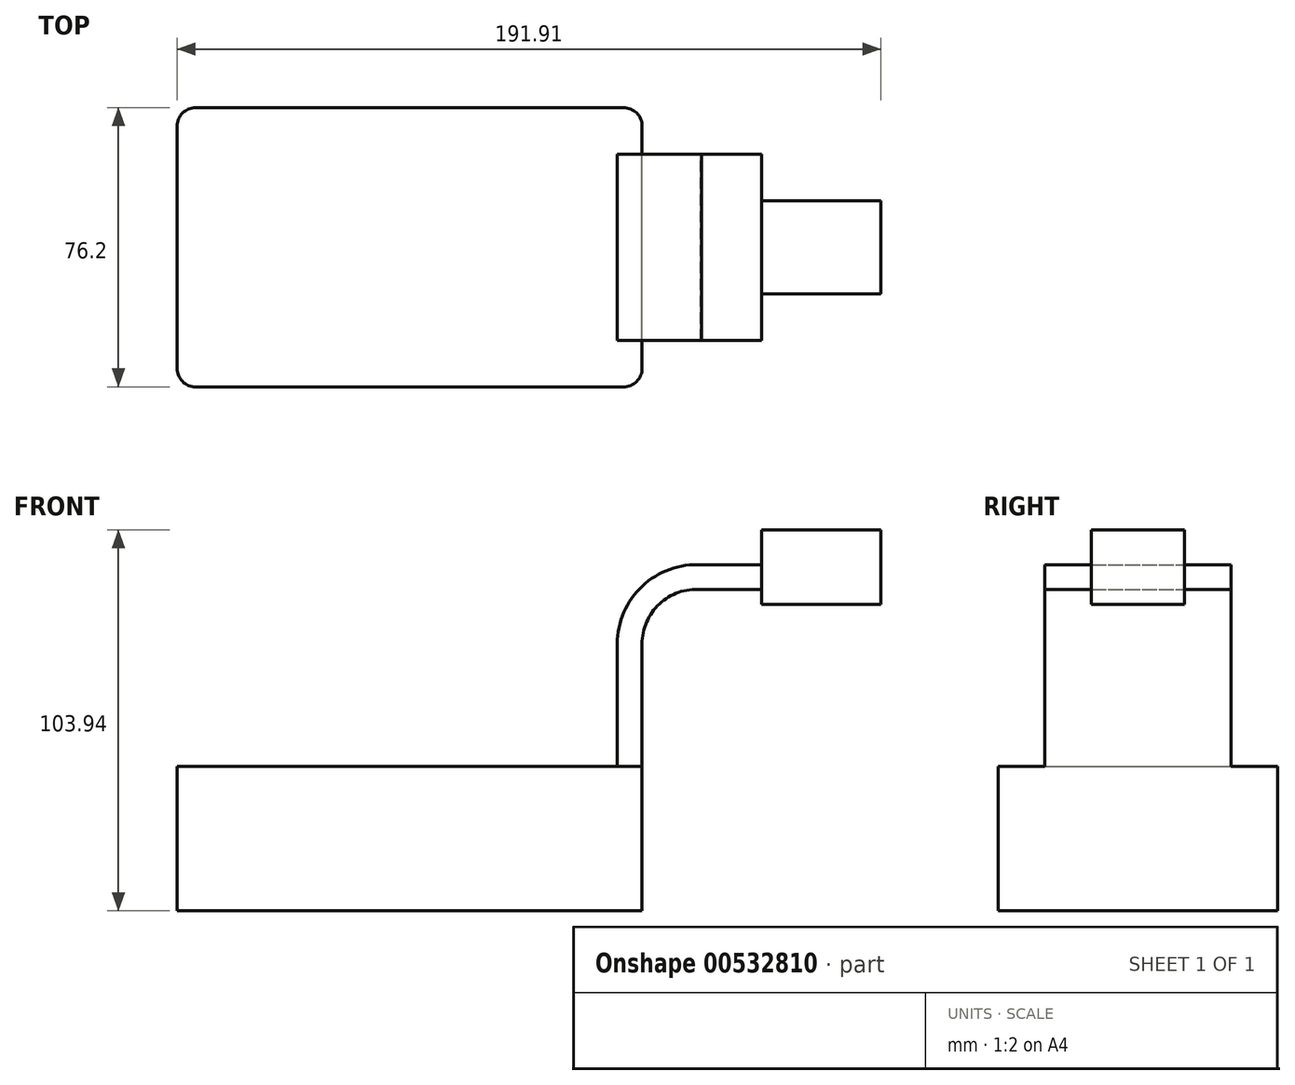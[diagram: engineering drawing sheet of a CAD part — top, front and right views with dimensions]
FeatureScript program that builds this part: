
annotation { "Feature Type Name" : "Feature", "Feature Type Description" : "" }
export const myFeature = defineFeature(function(context is Context, id is Id, definition is map)
    precondition{}
    {
        {
            var Q0;
            Q0=qCreatedBy(makeId("Front.planeOp"),FACE);
            var sketch = newSketch(context, id + "F0", { "sketchPlane" : qUnion([Q0])});
            skLineSegment(sketch, "E0.bottom", {"start": v(-63.4, -19.7) * mm, "end": v(63.4, -19.7) * mm});
            skLineSegment(sketch, "E0.top", {"start": v(-63.4, 19.7) * mm, "end": v(63.4, 19.7) * mm});
            skLineSegment(sketch, "E0.left", {"start": v(-63.4, -19.7) * mm, "end": v(-63.4, 19.7) * mm});
            skLineSegment(sketch, "E0.right", {"start": v(63.4, -19.7) * mm, "end": v(63.4, 19.7) * mm});
            skPoint(sketch, "E0.middle", {"position": v(0, 0) * mm});
            skLineSegment(sketch, "E1.bottom", {"start": v(95.95, 63.92) * mm, "end": v(128.5, 63.92) * mm});
            skLineSegment(sketch, "E1.top", {"start": v(95.95, 84.24) * mm, "end": v(128.5, 84.24) * mm});
            skLineSegment(sketch, "E1.left", {"start": v(95.95, 63.92) * mm, "end": v(95.95, 84.24) * mm});
            skLineSegment(sketch, "E1.right", {"start": v(128.5, 63.92) * mm, "end": v(128.5, 84.24) * mm});
            skPoint(sketch, "E1.middle", {"position": v(112.23, 74.08) * mm});
            skLineSegment(sketch, "E2", {"start": v(63.4, 19.7) * mm, "end": v(63.4, 53.12) * mm});
            skArc(sketch, "E3", {"start": v(63.4, 53.12) * mm, "mid": v(68.16, 64.03) * mm, "end": v(79.39, 67.97) * mm});
            skLineSegment(sketch, "E4", {"start": v(79.39, 67.97) * mm, "end": v(118.23, 67.97) * mm});
            skLineSegment(sketch, "E5.0", {"start": v(79.62, 74.71) * mm, "end": v(118.23, 74.71) * mm});
            skArc(sketch, "E5.1", {"start": v(56.65, 53.12) * mm, "mid": v(63.47, 68.88) * mm, "end": v(79.62, 74.71) * mm});
            skLineSegment(sketch, "E5.2", {"start": v(56.65, 19.7) * mm, "end": v(56.65, 53.12) * mm});
            skFitSpline(sketch, "E6", {"points": [v(-63.4, 19.7) * mm, v(95.95, 84.24) * mm], "startDerivative": vector(174.77, 0) * mm, "endDerivative": vector(220.18, -72.82) * mm});
            skSolve(sketch);
        }
        {
            var Q0;
            Q0=makeQuery(id+"F0.imprint","IMPRINT",FACE,{"disambiguationData":[TD([[makeQuery(id+"F0.imprint","IMPRINT",EDGE,{"derivedFrom":sQuery(id+"F0.wireOp",EDGE,"E0.bottom")}),1.0]])]});
            extrude(context, id + "F1", {"entities" : qUnion([Q0]), "endBound" : BoundingType.SYMMETRIC, "depth" : 76.2 * mm, "offsetDistance" : 25.4 * mm});
        }
        {
            var Q0;
            {var subQ0=sQuery(id+"F0.wireOp",EDGE,"E5.1");Q0=makeQuery(id+"F0.imprint","IMPRINT",FACE,{"disambiguationData":[TD([[makeQuery(id+"F0.imprint","IMPRINT",EDGE,{"derivedFrom":subQ0}),1.0]])]});}
            extrude(context, id + "F2", {"entities" : qUnion([Q0]), "operationType" : NewBodyOperationType.ADD, "endBound" : BoundingType.SYMMETRIC, "depth" : 50.8 * mm, "offsetDistance" : 25.4 * mm});
        }
        {
            var Q0;
            {var subQ0=sQuery(id+"F0.wireOp",EDGE,"E2");Q0=makeQuery(id+"F0.imprint","IMPRINT",FACE,{"disambiguationData":[TD([[makeQuery(id+"F0.imprint","IMPRINT",EDGE,{"derivedFrom":subQ0}),1.0]])]});}
            extrude(context, id + "F3", {"entities" : qUnion([Q0]), "operationType" : NewBodyOperationType.ADD, "endBound" : BoundingType.SYMMETRIC, "depth" : 25.4 * mm, "offsetDistance" : 25.4 * mm});
        }
        {
            var Q0;
            {var subQ3=sQuery(id+"F0.wireOp",EDGE,"E1.bottom");Q0=makeQuery(id+"F0.imprint","IMPRINT",FACE,{"disambiguationData":[TD([[makeQuery(id+"F0.imprint","IMPRINT",EDGE,{"derivedFrom":subQ3}),1.0]])]});}
            extrude(context, id + "F4", {"entities" : qUnion([Q0]), "operationType" : NewBodyOperationType.ADD, "endBound" : BoundingType.SYMMETRIC, "depth" : 25.4 * mm, "offsetDistance" : 25.4 * mm});
        }
        {
            var Q0;
            Q0=makeQuery(id+"F1.opExtrude","CAP_EDGE",EDGE,{"disambiguationData":[OSD([sQuery(id+"F0.wireOp",EDGE,"E0.left")])],"isStart":false});
            var Q1;
            Q1=makeQuery(id+"F1.opExtrude","CAP_EDGE",EDGE,{"disambiguationData":[OSD([sQuery(id+"F0.wireOp",EDGE,"E0.right")])],"isStart":false});
            var Q2;
            Q2=makeQuery(id+"F1.opExtrude","CAP_EDGE",EDGE,{"disambiguationData":[OSD([sQuery(id+"F0.wireOp",EDGE,"E0.right")])],"isStart":true});
            var Q3;
            Q3=makeQuery(id+"F1.opExtrude","CAP_EDGE",EDGE,{"disambiguationData":[OSD([sQuery(id+"F0.wireOp",EDGE,"E0.left")])],"isStart":true});
            fillet(context, id + "F5", {"entities" : qUnion([Q0, Q1, Q2, Q3]), "radius" : 5.08 * mm, "tangentPropagation" : true, "allowEdgeOverflow" : false});
        }
    });
